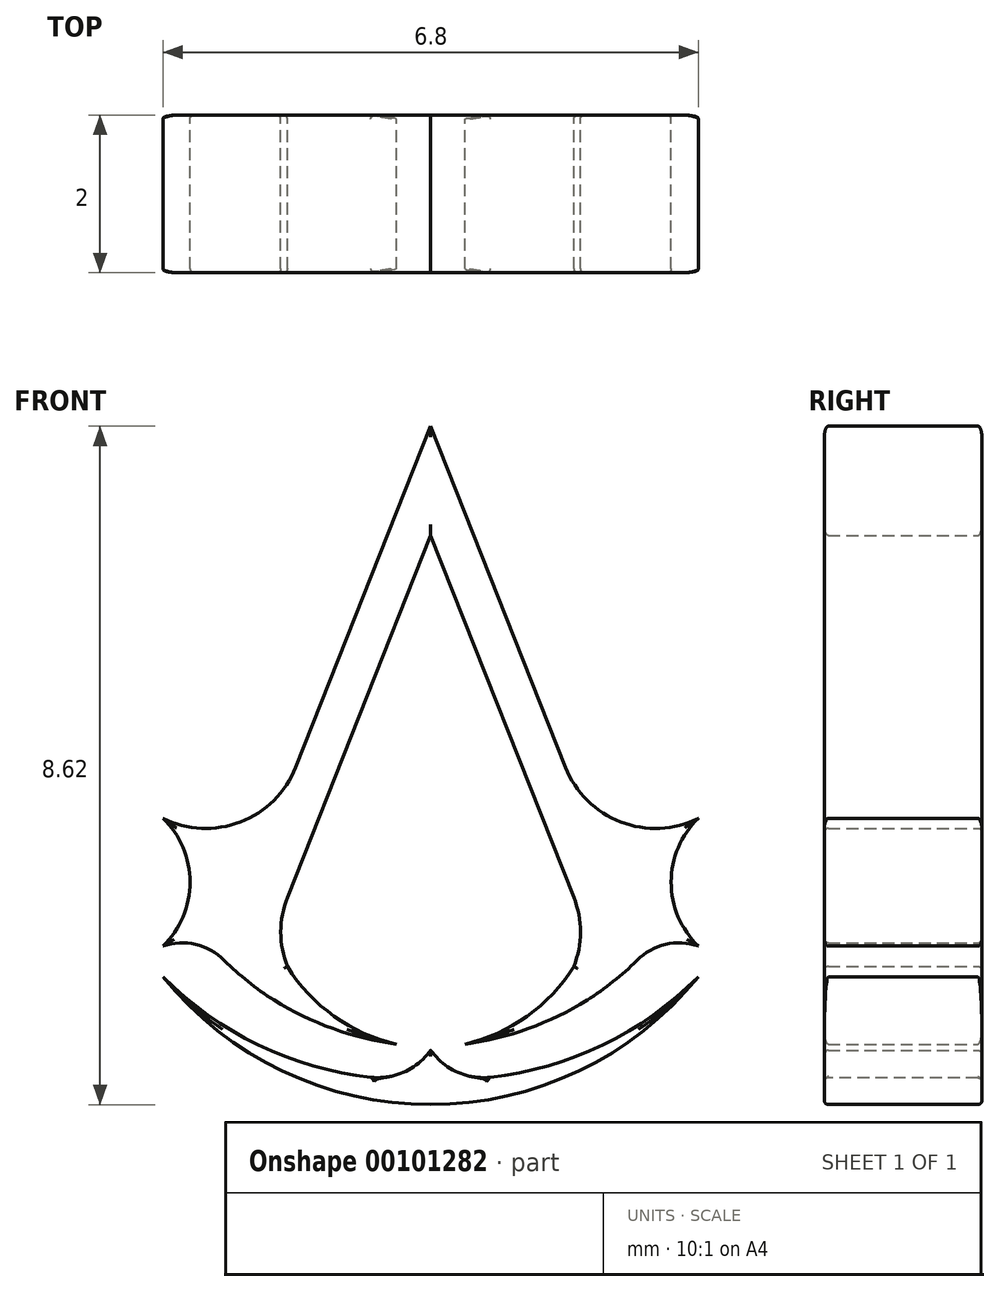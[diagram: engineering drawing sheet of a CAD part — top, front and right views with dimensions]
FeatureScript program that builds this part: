
annotation { "Feature Type Name" : "Feature", "Feature Type Description" : "" }
export const myFeature = defineFeature(function(context is Context, id is Id, definition is map)
    precondition{}
    {
        {
            var Q0;
            Q0=qCreatedBy(makeId("Front.planeOp"),FACE);
            var sketch = newSketch(context, id + "F0", { "sketchPlane" : qUnion([Q0])});
            skLineSegment(sketch, "E0", {"start": v(-3.75, 9.7) * mm, "end": v(-5.47, 5.38) * mm});
            skLineSegment(sketch, "E1", {"start": v(-3.75, 9.7) * mm, "end": v(-2.04, 5.38) * mm});
            skLineSegment(sketch, "E2", {"start": v(-3.75, 8.32) * mm, "end": v(-2.59, 5.38) * mm});
            skLineSegment(sketch, "E3", {"start": v(-3.75, 8.32) * mm, "end": v(-4.92, 5.38) * mm});
            skArc(sketch, "E4", {"start": v(-7.15, 4.73) * mm, "mid": v(-6.17, 4.68) * mm, "end": v(-5.47, 5.38) * mm});
            skArc(sketch, "E5", {"start": v(-2.04, 5.38) * mm, "mid": v(-1.34, 4.68) * mm, "end": v(-0.35, 4.73) * mm});
            skLineSegment(sketch, "E6", {"start": v(-4.92, 5.38) * mm, "end": v(-5.57, 3.72) * mm});
            skLineSegment(sketch, "E7", {"start": v(-2.59, 5.38) * mm, "end": v(-1.93, 3.72) * mm});
            skArc(sketch, "E8", {"start": v(-5.57, 3.72) * mm, "mid": v(-5.66, 3.28) * mm, "end": v(-5.57, 2.84) * mm});
            skArc(sketch, "E9", {"start": v(-1.93, 2.84) * mm, "mid": v(-1.85, 3.28) * mm, "end": v(-1.93, 3.72) * mm});
            skArc(sketch, "E10", {"start": v(-4.47, 1.43) * mm, "mid": v(-4.06, 1.52) * mm, "end": v(-3.75, 1.78) * mm});
            skArc(sketch, "E11", {"start": v(-3.75, 1.78) * mm, "mid": v(-3.44, 1.52) * mm, "end": v(-3.04, 1.43) * mm});
            skArc(sketch, "E12", {"start": v(-7.15, 2.72) * mm, "mid": v(-5.92, 1.84) * mm, "end": v(-4.47, 1.43) * mm});
            skArc(sketch, "E13", {"start": v(-3.04, 1.43) * mm, "mid": v(-1.58, 1.84) * mm, "end": v(-0.35, 2.72) * mm});
            skArc(sketch, "E14", {"start": v(-7.15, 2.72) * mm, "mid": v(-3.75, 1.1) * mm, "end": v(-0.35, 2.72) * mm});
            skArc(sketch, "E15", {"start": v(-6.3, 2.84) * mm, "mid": v(-6.69, 3.11) * mm, "end": v(-7.15, 3.1) * mm});
            skArc(sketch, "E16", {"start": v(-0.35, 3.1) * mm, "mid": v(-0.82, 3.11) * mm, "end": v(-1.2, 2.84) * mm});
            skArc(sketch, "E17", {"start": v(-6.3, 2.84) * mm, "mid": v(-5.32, 2.2) * mm, "end": v(-4.19, 1.86) * mm});
            skArc(sketch, "E18", {"start": v(-3.32, 1.86) * mm, "mid": v(-2.18, 2.2) * mm, "end": v(-1.2, 2.84) * mm});
            skArc(sketch, "E19", {"start": v(-5.57, 2.84) * mm, "mid": v(-4.98, 2.21) * mm, "end": v(-4.19, 1.86) * mm});
            skArc(sketch, "E20", {"start": v(-3.32, 1.86) * mm, "mid": v(-2.53, 2.21) * mm, "end": v(-1.93, 2.84) * mm});
            skArc(sketch, "E21", {"start": v(-7.15, 3.1) * mm, "mid": v(-6.8, 3.92) * mm, "end": v(-7.15, 4.73) * mm});
            skArc(sketch, "E22", {"start": v(-0.35, 4.73) * mm, "mid": v(-0.7, 3.92) * mm, "end": v(-0.35, 3.1) * mm});
            skSolve(sketch);
        }
        {
            var Q0;
            Q0=makeQuery(id+"F0.imprint","IMPRINT",FACE,{"disambiguationData":[TD([[makeQuery(id+"F0.imprint","IMPRINT",EDGE,{"derivedFrom":sQuery(id+"F0.wireOp",EDGE,"E0")}),1.0]])]});
            var Q1;
            Q1=makeQuery(id+"F0.imprint","IMPRINT",FACE,{"disambiguationData":[TD([[makeQuery(id+"F0.imprint","IMPRINT",EDGE,{"derivedFrom":sQuery(id+"F0.wireOp",EDGE,"E10")}),-1.0]])]});
            extrude(context, id + "F1", {"entities" : qUnion([Q0, Q1]), "depth" : 2 * mm});
        }
        {
            var Q0;
            Q0=makeQuery(id+"F1.opExtrude","SWEPT_EDGE",EDGE,{"disambiguationData":[OSD([sQuery(id+"F0.wireOp",EDGE,"E15"),sQuery(id+"F0.wireOp",EDGE,"E17")])]});
            var Q1;
            Q1=makeQuery(id+"F1.opExtrude","SWEPT_EDGE",EDGE,{"disambiguationData":[OSD([sQuery(id+"F0.wireOp",EDGE,"E16"),sQuery(id+"F0.wireOp",EDGE,"E18")])]});
            fillet(context, id + "F2", {"entities" : qUnion([Q0, Q1]), "radius" : 3.5 * mm, "allowEdgeOverflow" : false});
        }
        {
            var Q0;
            Q0=makeQuery(id+"F1.opExtrude","CAP_EDGE",EDGE,{"disambiguationData":[OSD([sQuery(id+"F0.wireOp",EDGE,"E0")])],"isStart":false});
            var Q1;
            Q1=makeQuery(id+"F1.opExtrude","CAP_EDGE",EDGE,{"disambiguationData":[OSD([sQuery(id+"F0.wireOp",EDGE,"E3"),sQuery(id+"F0.wireOp",EDGE,"E6")])],"isStart":false});
            var Q2;
            Q2=makeQuery(id+"F1.opExtrude","CAP_EDGE",EDGE,{"disambiguationData":[OSD([sQuery(id+"F0.wireOp",EDGE,"E2"),sQuery(id+"F0.wireOp",EDGE,"E7")])],"isStart":false});
            var Q3;
            Q3=makeQuery(id+"F1.opExtrude","CAP_EDGE",EDGE,{"disambiguationData":[OSD([sQuery(id+"F0.wireOp",EDGE,"E1")])],"isStart":false});
            var Q4;
            Q4=makeQuery(id+"F1.opExtrude","CAP_EDGE",EDGE,{"disambiguationData":[OSD([sQuery(id+"F0.wireOp",EDGE,"E4")])],"isStart":false});
            var Q5;
            Q5=makeQuery(id+"F1.opExtrude","CAP_EDGE",EDGE,{"disambiguationData":[OSD([sQuery(id+"F0.wireOp",EDGE,"wj90hjxO-9zCW-fV7Z-uJP1-WtdDD03QQXYp")])],"isStart":false});
            var Q6;
            Q6=makeQuery(id+"F1.opExtrude","CAP_EDGE",EDGE,{"disambiguationData":[OSD([sQuery(id+"F0.wireOp",EDGE,"E15")])],"isStart":false});
            var Q7;
            {var subQ0=sQuery(id+"F0.wireOp",EDGE,"E17");var subQ1=sQuery(id+"F0.wireOp",EDGE,"E15");Q7=makeQuery(id+"F2.opFillet","BLEND_EDGE",EDGE,{"blendedFrom":[makeQuery(id+"F1.opExtrude","SWEPT_EDGE",EDGE,{"disambiguationData":[OSD([subQ1,subQ0])]}),makeQuery(id+"F1.opExtrude","CAP_FACE",FACE,{"disambiguationData":[OSD([sQuery(id+"F0.wireOp",EDGE,"E0"),sQuery(id+"F0.wireOp",EDGE,"E1"),sQuery(id+"F0.wireOp",EDGE,"E2"),sQuery(id+"F0.wireOp",EDGE,"E3"),sQuery(id+"F0.wireOp",EDGE,"E4"),sQuery(id+"F0.wireOp",EDGE,"E5"),sQuery(id+"F0.wireOp",EDGE,"E6"),sQuery(id+"F0.wireOp",EDGE,"E7"),sQuery(id+"F0.wireOp",EDGE,"E8"),sQuery(id+"F0.wireOp",EDGE,"E9"),sQuery(id+"F0.wireOp",EDGE,"wj90hjxO-9zCW-fV7Z-uJP1-WtdDD03QQXYp"),sQuery(id+"F0.wireOp",EDGE,"czgwStC1-4lpA-qfDe-yVWo-KE0qLoUrKhMa"),subQ1,sQuery(id+"F0.wireOp",EDGE,"E16"),subQ0,sQuery(id+"F0.wireOp",EDGE,"E18"),sQuery(id+"F0.wireOp",EDGE,"E19"),sQuery(id+"F0.wireOp",EDGE,"E20")])],"isStart":false})],"blendedInto":[makeQuery(id+"F1.opExtrude","CAP_FACE",FACE,{"disambiguationData":[OSD([sQuery(id+"F0.wireOp",EDGE,"E0"),sQuery(id+"F0.wireOp",EDGE,"E1"),sQuery(id+"F0.wireOp",EDGE,"E2"),sQuery(id+"F0.wireOp",EDGE,"E3"),sQuery(id+"F0.wireOp",EDGE,"E4"),sQuery(id+"F0.wireOp",EDGE,"E5"),sQuery(id+"F0.wireOp",EDGE,"E6"),sQuery(id+"F0.wireOp",EDGE,"E7"),sQuery(id+"F0.wireOp",EDGE,"E8"),sQuery(id+"F0.wireOp",EDGE,"E9"),sQuery(id+"F0.wireOp",EDGE,"wj90hjxO-9zCW-fV7Z-uJP1-WtdDD03QQXYp"),sQuery(id+"F0.wireOp",EDGE,"czgwStC1-4lpA-qfDe-yVWo-KE0qLoUrKhMa"),subQ1,sQuery(id+"F0.wireOp",EDGE,"E16"),subQ0,sQuery(id+"F0.wireOp",EDGE,"E18"),sQuery(id+"F0.wireOp",EDGE,"E19"),sQuery(id+"F0.wireOp",EDGE,"E20")])],"isStart":false})]});}
            var Q8;
            Q8=makeQuery(id+"F1.opExtrude","CAP_EDGE",EDGE,{"disambiguationData":[OSD([sQuery(id+"F0.wireOp",EDGE,"E17")])],"isStart":false});
            var Q9;
            {var subQ0=sQuery(id+"F0.wireOp",EDGE,"E17");var subQ1=sQuery(id+"F0.wireOp",EDGE,"E15");Q9=makeQuery(id+"F2.opFillet","BLEND_EDGE",EDGE,{"blendedFrom":[makeQuery(id+"F1.opExtrude","SWEPT_EDGE",EDGE,{"disambiguationData":[OSD([subQ1,subQ0])]}),makeQuery(id+"F1.opExtrude","CAP_FACE",FACE,{"disambiguationData":[OSD([sQuery(id+"F0.wireOp",EDGE,"E0"),sQuery(id+"F0.wireOp",EDGE,"E1"),sQuery(id+"F0.wireOp",EDGE,"E2"),sQuery(id+"F0.wireOp",EDGE,"E3"),sQuery(id+"F0.wireOp",EDGE,"E4"),sQuery(id+"F0.wireOp",EDGE,"E5"),sQuery(id+"F0.wireOp",EDGE,"E6"),sQuery(id+"F0.wireOp",EDGE,"E7"),sQuery(id+"F0.wireOp",EDGE,"E8"),sQuery(id+"F0.wireOp",EDGE,"E9"),sQuery(id+"F0.wireOp",EDGE,"wj90hjxO-9zCW-fV7Z-uJP1-WtdDD03QQXYp"),sQuery(id+"F0.wireOp",EDGE,"czgwStC1-4lpA-qfDe-yVWo-KE0qLoUrKhMa"),subQ1,sQuery(id+"F0.wireOp",EDGE,"E16"),subQ0,sQuery(id+"F0.wireOp",EDGE,"E18"),sQuery(id+"F0.wireOp",EDGE,"E19"),sQuery(id+"F0.wireOp",EDGE,"E20")])],"isStart":false})],"blendedInto":[makeQuery(id+"F1.opExtrude","CAP_FACE",FACE,{"disambiguationData":[OSD([sQuery(id+"F0.wireOp",EDGE,"E0"),sQuery(id+"F0.wireOp",EDGE,"E1"),sQuery(id+"F0.wireOp",EDGE,"E2"),sQuery(id+"F0.wireOp",EDGE,"E3"),sQuery(id+"F0.wireOp",EDGE,"E4"),sQuery(id+"F0.wireOp",EDGE,"E5"),sQuery(id+"F0.wireOp",EDGE,"E6"),sQuery(id+"F0.wireOp",EDGE,"E7"),sQuery(id+"F0.wireOp",EDGE,"E8"),sQuery(id+"F0.wireOp",EDGE,"E9"),sQuery(id+"F0.wireOp",EDGE,"wj90hjxO-9zCW-fV7Z-uJP1-WtdDD03QQXYp"),sQuery(id+"F0.wireOp",EDGE,"czgwStC1-4lpA-qfDe-yVWo-KE0qLoUrKhMa"),subQ1,sQuery(id+"F0.wireOp",EDGE,"E16"),subQ0,sQuery(id+"F0.wireOp",EDGE,"E18"),sQuery(id+"F0.wireOp",EDGE,"E19"),sQuery(id+"F0.wireOp",EDGE,"E20")])],"isStart":false})]});}
            var Q10;
            Q10=makeQuery(id+"F1.opExtrude","CAP_EDGE",EDGE,{"disambiguationData":[OSD([sQuery(id+"F0.wireOp",EDGE,"E8")])],"isStart":false});
            var Q11;
            Q11=makeQuery(id+"F1.opExtrude","CAP_EDGE",EDGE,{"disambiguationData":[OSD([sQuery(id+"F0.wireOp",EDGE,"E19")])],"isStart":false});
            var Q12;
            Q12=makeQuery(id+"F1.opExtrude","CAP_EDGE",EDGE,{"disambiguationData":[OSD([sQuery(id+"F0.wireOp",EDGE,"E20")])],"isStart":false});
            var Q13;
            Q13=makeQuery(id+"F1.opExtrude","CAP_EDGE",EDGE,{"disambiguationData":[OSD([sQuery(id+"F0.wireOp",EDGE,"E18")])],"isStart":false});
            var Q14;
            Q14=makeQuery(id+"F1.opExtrude","CAP_EDGE",EDGE,{"disambiguationData":[OSD([sQuery(id+"F0.wireOp",EDGE,"E9")])],"isStart":false});
            var Q15;
            Q15=makeQuery(id+"F1.opExtrude","CAP_EDGE",EDGE,{"disambiguationData":[OSD([sQuery(id+"F0.wireOp",EDGE,"E16")])],"isStart":false});
            var Q16;
            {var subQ0=sQuery(id+"F0.wireOp",EDGE,"E18");var subQ1=sQuery(id+"F0.wireOp",EDGE,"E16");Q16=makeQuery(id+"F2.opFillet","BLEND_EDGE",EDGE,{"blendedFrom":[makeQuery(id+"F1.opExtrude","SWEPT_EDGE",EDGE,{"disambiguationData":[OSD([subQ1,subQ0])]}),makeQuery(id+"F1.opExtrude","CAP_FACE",FACE,{"disambiguationData":[OSD([sQuery(id+"F0.wireOp",EDGE,"E0"),sQuery(id+"F0.wireOp",EDGE,"E1"),sQuery(id+"F0.wireOp",EDGE,"E2"),sQuery(id+"F0.wireOp",EDGE,"E3"),sQuery(id+"F0.wireOp",EDGE,"E4"),sQuery(id+"F0.wireOp",EDGE,"E5"),sQuery(id+"F0.wireOp",EDGE,"E6"),sQuery(id+"F0.wireOp",EDGE,"E7"),sQuery(id+"F0.wireOp",EDGE,"E8"),sQuery(id+"F0.wireOp",EDGE,"E9"),sQuery(id+"F0.wireOp",EDGE,"wj90hjxO-9zCW-fV7Z-uJP1-WtdDD03QQXYp"),sQuery(id+"F0.wireOp",EDGE,"czgwStC1-4lpA-qfDe-yVWo-KE0qLoUrKhMa"),sQuery(id+"F0.wireOp",EDGE,"E15"),subQ1,sQuery(id+"F0.wireOp",EDGE,"E17"),subQ0,sQuery(id+"F0.wireOp",EDGE,"E19"),sQuery(id+"F0.wireOp",EDGE,"E20")])],"isStart":false})],"blendedInto":[makeQuery(id+"F1.opExtrude","CAP_FACE",FACE,{"disambiguationData":[OSD([sQuery(id+"F0.wireOp",EDGE,"E0"),sQuery(id+"F0.wireOp",EDGE,"E1"),sQuery(id+"F0.wireOp",EDGE,"E2"),sQuery(id+"F0.wireOp",EDGE,"E3"),sQuery(id+"F0.wireOp",EDGE,"E4"),sQuery(id+"F0.wireOp",EDGE,"E5"),sQuery(id+"F0.wireOp",EDGE,"E6"),sQuery(id+"F0.wireOp",EDGE,"E7"),sQuery(id+"F0.wireOp",EDGE,"E8"),sQuery(id+"F0.wireOp",EDGE,"E9"),sQuery(id+"F0.wireOp",EDGE,"wj90hjxO-9zCW-fV7Z-uJP1-WtdDD03QQXYp"),sQuery(id+"F0.wireOp",EDGE,"czgwStC1-4lpA-qfDe-yVWo-KE0qLoUrKhMa"),sQuery(id+"F0.wireOp",EDGE,"E15"),subQ1,sQuery(id+"F0.wireOp",EDGE,"E17"),subQ0,sQuery(id+"F0.wireOp",EDGE,"E19"),sQuery(id+"F0.wireOp",EDGE,"E20")])],"isStart":false})]});}
            var Q17;
            Q17=makeQuery(id+"F1.opExtrude","CAP_EDGE",EDGE,{"disambiguationData":[OSD([sQuery(id+"F0.wireOp",EDGE,"czgwStC1-4lpA-qfDe-yVWo-KE0qLoUrKhMa")])],"isStart":false});
            var Q18;
            Q18=makeQuery(id+"F1.opExtrude","CAP_EDGE",EDGE,{"disambiguationData":[OSD([sQuery(id+"F0.wireOp",EDGE,"E5")])],"isStart":false});
            var Q19;
            Q19=makeQuery(id+"F1.opExtrude","CAP_EDGE",EDGE,{"disambiguationData":[OSD([sQuery(id+"F0.wireOp",EDGE,"E12")])],"isStart":false});
            var Q20;
            Q20=makeQuery(id+"F1.opExtrude","CAP_EDGE",EDGE,{"disambiguationData":[OSD([sQuery(id+"F0.wireOp",EDGE,"E10")])],"isStart":false});
            var Q21;
            Q21=makeQuery(id+"F1.opExtrude","CAP_EDGE",EDGE,{"disambiguationData":[OSD([sQuery(id+"F0.wireOp",EDGE,"E11")])],"isStart":false});
            var Q22;
            Q22=makeQuery(id+"F1.opExtrude","CAP_EDGE",EDGE,{"disambiguationData":[OSD([sQuery(id+"F0.wireOp",EDGE,"E13")])],"isStart":false});
            var Q23;
            Q23=makeQuery(id+"F1.opExtrude","CAP_EDGE",EDGE,{"disambiguationData":[OSD([sQuery(id+"F0.wireOp",EDGE,"E14")])],"isStart":false});
            var Q24;
            Q24=makeQuery(id+"F1.opExtrude","CAP_EDGE",EDGE,{"disambiguationData":[OSD([sQuery(id+"F0.wireOp",EDGE,"E1")])],"isStart":true});
            var Q25;
            Q25=makeQuery(id+"F1.opExtrude","CAP_EDGE",EDGE,{"disambiguationData":[OSD([sQuery(id+"F0.wireOp",EDGE,"E2"),sQuery(id+"F0.wireOp",EDGE,"E7")])],"isStart":true});
            var Q26;
            Q26=makeQuery(id+"F1.opExtrude","CAP_EDGE",EDGE,{"disambiguationData":[OSD([sQuery(id+"F0.wireOp",EDGE,"E3"),sQuery(id+"F0.wireOp",EDGE,"E6")])],"isStart":true});
            var Q27;
            Q27=makeQuery(id+"F1.opExtrude","CAP_EDGE",EDGE,{"disambiguationData":[OSD([sQuery(id+"F0.wireOp",EDGE,"E0")])],"isStart":true});
            var Q28;
            Q28=makeQuery(id+"F1.opExtrude","CAP_EDGE",EDGE,{"disambiguationData":[OSD([sQuery(id+"F0.wireOp",EDGE,"E4")])],"isStart":true});
            var Q29;
            Q29=makeQuery(id+"F1.opExtrude","CAP_EDGE",EDGE,{"disambiguationData":[OSD([sQuery(id+"F0.wireOp",EDGE,"wj90hjxO-9zCW-fV7Z-uJP1-WtdDD03QQXYp")])],"isStart":true});
            var Q30;
            Q30=makeQuery(id+"F1.opExtrude","CAP_EDGE",EDGE,{"disambiguationData":[OSD([sQuery(id+"F0.wireOp",EDGE,"E15")])],"isStart":true});
            var Q31;
            {var subQ0=sQuery(id+"F0.wireOp",EDGE,"E17");var subQ1=sQuery(id+"F0.wireOp",EDGE,"E15");Q31=makeQuery(id+"F2.opFillet","BLEND_EDGE",EDGE,{"blendedFrom":[makeQuery(id+"F1.opExtrude","SWEPT_EDGE",EDGE,{"disambiguationData":[OSD([subQ1,subQ0])]}),makeQuery(id+"F1.opExtrude","CAP_FACE",FACE,{"disambiguationData":[OSD([sQuery(id+"F0.wireOp",EDGE,"E0"),sQuery(id+"F0.wireOp",EDGE,"E1"),sQuery(id+"F0.wireOp",EDGE,"E2"),sQuery(id+"F0.wireOp",EDGE,"E3"),sQuery(id+"F0.wireOp",EDGE,"E4"),sQuery(id+"F0.wireOp",EDGE,"E5"),sQuery(id+"F0.wireOp",EDGE,"E6"),sQuery(id+"F0.wireOp",EDGE,"E7"),sQuery(id+"F0.wireOp",EDGE,"E8"),sQuery(id+"F0.wireOp",EDGE,"E9"),sQuery(id+"F0.wireOp",EDGE,"wj90hjxO-9zCW-fV7Z-uJP1-WtdDD03QQXYp"),sQuery(id+"F0.wireOp",EDGE,"czgwStC1-4lpA-qfDe-yVWo-KE0qLoUrKhMa"),subQ1,sQuery(id+"F0.wireOp",EDGE,"E16"),subQ0,sQuery(id+"F0.wireOp",EDGE,"E18"),sQuery(id+"F0.wireOp",EDGE,"E19"),sQuery(id+"F0.wireOp",EDGE,"E20")])],"isStart":true})],"blendedInto":[makeQuery(id+"F1.opExtrude","CAP_FACE",FACE,{"disambiguationData":[OSD([sQuery(id+"F0.wireOp",EDGE,"E0"),sQuery(id+"F0.wireOp",EDGE,"E1"),sQuery(id+"F0.wireOp",EDGE,"E2"),sQuery(id+"F0.wireOp",EDGE,"E3"),sQuery(id+"F0.wireOp",EDGE,"E4"),sQuery(id+"F0.wireOp",EDGE,"E5"),sQuery(id+"F0.wireOp",EDGE,"E6"),sQuery(id+"F0.wireOp",EDGE,"E7"),sQuery(id+"F0.wireOp",EDGE,"E8"),sQuery(id+"F0.wireOp",EDGE,"E9"),sQuery(id+"F0.wireOp",EDGE,"wj90hjxO-9zCW-fV7Z-uJP1-WtdDD03QQXYp"),sQuery(id+"F0.wireOp",EDGE,"czgwStC1-4lpA-qfDe-yVWo-KE0qLoUrKhMa"),subQ1,sQuery(id+"F0.wireOp",EDGE,"E16"),subQ0,sQuery(id+"F0.wireOp",EDGE,"E18"),sQuery(id+"F0.wireOp",EDGE,"E19"),sQuery(id+"F0.wireOp",EDGE,"E20")])],"isStart":true})]});}
            var Q32;
            Q32=makeQuery(id+"F1.opExtrude","CAP_EDGE",EDGE,{"disambiguationData":[OSD([sQuery(id+"F0.wireOp",EDGE,"E17")])],"isStart":true});
            var Q33;
            Q33=makeQuery(id+"F1.opExtrude","CAP_EDGE",EDGE,{"disambiguationData":[OSD([sQuery(id+"F0.wireOp",EDGE,"E9")])],"isStart":true});
            var Q34;
            Q34=makeQuery(id+"F1.opExtrude","CAP_EDGE",EDGE,{"disambiguationData":[OSD([sQuery(id+"F0.wireOp",EDGE,"E20")])],"isStart":true});
            var Q35;
            Q35=makeQuery(id+"F1.opExtrude","CAP_EDGE",EDGE,{"disambiguationData":[OSD([sQuery(id+"F0.wireOp",EDGE,"E5")])],"isStart":true});
            var Q36;
            Q36=makeQuery(id+"F1.opExtrude","CAP_EDGE",EDGE,{"disambiguationData":[OSD([sQuery(id+"F0.wireOp",EDGE,"czgwStC1-4lpA-qfDe-yVWo-KE0qLoUrKhMa")])],"isStart":true});
            var Q37;
            Q37=makeQuery(id+"F1.opExtrude","CAP_EDGE",EDGE,{"disambiguationData":[OSD([sQuery(id+"F0.wireOp",EDGE,"E16")])],"isStart":true});
            var Q38;
            {var subQ0=sQuery(id+"F0.wireOp",EDGE,"E18");var subQ1=sQuery(id+"F0.wireOp",EDGE,"E16");Q38=makeQuery(id+"F2.opFillet","BLEND_EDGE",EDGE,{"blendedFrom":[makeQuery(id+"F1.opExtrude","SWEPT_EDGE",EDGE,{"disambiguationData":[OSD([subQ1,subQ0])]}),makeQuery(id+"F1.opExtrude","CAP_FACE",FACE,{"disambiguationData":[OSD([sQuery(id+"F0.wireOp",EDGE,"E0"),sQuery(id+"F0.wireOp",EDGE,"E1"),sQuery(id+"F0.wireOp",EDGE,"E2"),sQuery(id+"F0.wireOp",EDGE,"E3"),sQuery(id+"F0.wireOp",EDGE,"E4"),sQuery(id+"F0.wireOp",EDGE,"E5"),sQuery(id+"F0.wireOp",EDGE,"E6"),sQuery(id+"F0.wireOp",EDGE,"E7"),sQuery(id+"F0.wireOp",EDGE,"E8"),sQuery(id+"F0.wireOp",EDGE,"E9"),sQuery(id+"F0.wireOp",EDGE,"wj90hjxO-9zCW-fV7Z-uJP1-WtdDD03QQXYp"),sQuery(id+"F0.wireOp",EDGE,"czgwStC1-4lpA-qfDe-yVWo-KE0qLoUrKhMa"),sQuery(id+"F0.wireOp",EDGE,"E15"),subQ1,sQuery(id+"F0.wireOp",EDGE,"E17"),subQ0,sQuery(id+"F0.wireOp",EDGE,"E19"),sQuery(id+"F0.wireOp",EDGE,"E20")])],"isStart":true})],"blendedInto":[makeQuery(id+"F1.opExtrude","CAP_FACE",FACE,{"disambiguationData":[OSD([sQuery(id+"F0.wireOp",EDGE,"E0"),sQuery(id+"F0.wireOp",EDGE,"E1"),sQuery(id+"F0.wireOp",EDGE,"E2"),sQuery(id+"F0.wireOp",EDGE,"E3"),sQuery(id+"F0.wireOp",EDGE,"E4"),sQuery(id+"F0.wireOp",EDGE,"E5"),sQuery(id+"F0.wireOp",EDGE,"E6"),sQuery(id+"F0.wireOp",EDGE,"E7"),sQuery(id+"F0.wireOp",EDGE,"E8"),sQuery(id+"F0.wireOp",EDGE,"E9"),sQuery(id+"F0.wireOp",EDGE,"wj90hjxO-9zCW-fV7Z-uJP1-WtdDD03QQXYp"),sQuery(id+"F0.wireOp",EDGE,"czgwStC1-4lpA-qfDe-yVWo-KE0qLoUrKhMa"),sQuery(id+"F0.wireOp",EDGE,"E15"),subQ1,sQuery(id+"F0.wireOp",EDGE,"E17"),subQ0,sQuery(id+"F0.wireOp",EDGE,"E19"),sQuery(id+"F0.wireOp",EDGE,"E20")])],"isStart":true})]});}
            var Q39;
            Q39=makeQuery(id+"F1.opExtrude","CAP_EDGE",EDGE,{"disambiguationData":[OSD([sQuery(id+"F0.wireOp",EDGE,"E18")])],"isStart":true});
            var Q40;
            Q40=makeQuery(id+"F1.opExtrude","CAP_EDGE",EDGE,{"disambiguationData":[OSD([sQuery(id+"F0.wireOp",EDGE,"E19")])],"isStart":true});
            var Q41;
            Q41=makeQuery(id+"F1.opExtrude","CAP_EDGE",EDGE,{"disambiguationData":[OSD([sQuery(id+"F0.wireOp",EDGE,"E8")])],"isStart":true});
            var Q42;
            Q42=makeQuery(id+"F1.opExtrude","CAP_EDGE",EDGE,{"disambiguationData":[OSD([sQuery(id+"F0.wireOp",EDGE,"E13")])],"isStart":true});
            var Q43;
            Q43=makeQuery(id+"F1.opExtrude","CAP_EDGE",EDGE,{"disambiguationData":[OSD([sQuery(id+"F0.wireOp",EDGE,"E11")])],"isStart":true});
            var Q44;
            Q44=makeQuery(id+"F1.opExtrude","CAP_EDGE",EDGE,{"disambiguationData":[OSD([sQuery(id+"F0.wireOp",EDGE,"E10")])],"isStart":true});
            var Q45;
            Q45=makeQuery(id+"F1.opExtrude","CAP_EDGE",EDGE,{"disambiguationData":[OSD([sQuery(id+"F0.wireOp",EDGE,"E12")])],"isStart":true});
            var Q46;
            Q46=makeQuery(id+"F1.opExtrude","CAP_EDGE",EDGE,{"disambiguationData":[OSD([sQuery(id+"F0.wireOp",EDGE,"E14")])],"isStart":true});
            var Q47;
            Q47=makeQuery(id+"F1.opExtrude","CAP_EDGE",EDGE,{"disambiguationData":[OSD([sQuery(id+"F0.wireOp",EDGE,"E21")])],"isStart":false});
            var Q48;
            Q48=makeQuery(id+"F1.opExtrude","CAP_EDGE",EDGE,{"disambiguationData":[OSD([sQuery(id+"F0.wireOp",EDGE,"E21")])],"isStart":true});
            var Q49;
            Q49=makeQuery(id+"F1.opExtrude","CAP_EDGE",EDGE,{"disambiguationData":[OSD([sQuery(id+"F0.wireOp",EDGE,"E22")])],"isStart":true});
            var Q50;
            Q50=makeQuery(id+"F1.opExtrude","CAP_EDGE",EDGE,{"disambiguationData":[OSD([sQuery(id+"F0.wireOp",EDGE,"E22")])],"isStart":false});
            fillet(context, id + "F3", {"entities" : qUnion([Q0, Q1, Q2, Q3, Q4, Q5, Q6, Q7, Q8, Q9, Q10, Q11, Q12, Q13, Q14, Q15, Q16, Q17, Q18, Q19, Q20, Q21, Q22, Q23, Q24, Q25, Q26, Q27, Q28, Q29, Q30, Q31, Q32, Q33, Q34, Q35, Q36, Q37, Q38, Q39, Q40, Q41, Q42, Q43, Q44, Q45, Q46, Q47, Q48, Q49, Q50]), "radius" : 0.05 * mm, "tangentPropagation" : true, "allowEdgeOverflow" : false});
        }
        {
            var Q0;
            Q0=makeQuery(id+"F1.opExtrude","SWEPT_EDGE",EDGE,{"disambiguationData":[OSD([sQuery(id+"F0.wireOp",EDGE,"E10"),sQuery(id+"F0.wireOp",EDGE,"E12")])]});
            var Q1;
            Q1=makeQuery(id+"F1.opExtrude","SWEPT_EDGE",EDGE,{"disambiguationData":[OSD([sQuery(id+"F0.wireOp",EDGE,"E11"),sQuery(id+"F0.wireOp",EDGE,"E13")])]});
            fillet(context, id + "F4", {"entities" : qUnion([Q0, Q1]), "radius" : 0.8 * mm, "tangentPropagation" : true, "allowEdgeOverflow" : false});
        }
    });
